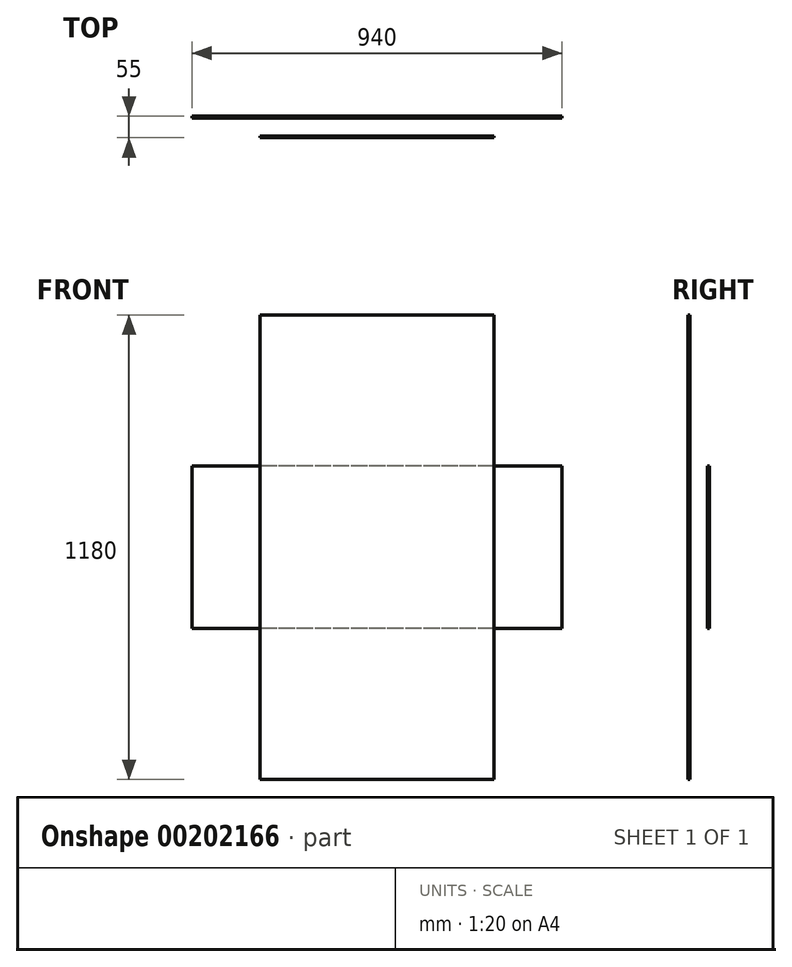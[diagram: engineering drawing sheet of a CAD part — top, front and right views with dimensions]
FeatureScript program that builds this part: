
annotation { "Feature Type Name" : "Feature", "Feature Type Description" : "" }
export const myFeature = defineFeature(function(context is Context, id is Id, definition is map)
    precondition{}
    {
        {
            var Q0;
            Q0=qCreatedBy(makeId("Front.planeOp"),FACE);
            var sketch = newSketch(context, id + "F0", { "sketchPlane" : qUnion([Q0])});
            skLineSegment(sketch, "E0.bottom", {"start": v(470, 206) * mm, "end": v(-470, 206) * mm});
            skLineSegment(sketch, "E0.top", {"start": v(470, -206) * mm, "end": v(-470, -206) * mm});
            skLineSegment(sketch, "E0.left", {"start": v(470, 206) * mm, "end": v(470, -206) * mm});
            skLineSegment(sketch, "E0.right", {"start": v(-470, 206) * mm, "end": v(-470, -206) * mm});
            skPoint(sketch, "E0.middle", {"position": v(0, 0) * mm});
            skSolve(sketch);
        }
        {
            var Q0;
            Q0=qSketchRegion(id+"F0",true);
            extrude(context, id + "F1", {"entities" : qUnion([Q0]), "depth" : 5 * mm});
        }
        {
            var Q0;
            Q0=qCreatedBy(makeId("Front.planeOp"),FACE);
            cPlane(context, id + "F2", {"entities" : qUnion([Q0]), "cplaneType" : CPlaneType.OFFSET, "offset" : 50 * mm, "width" : 150 * mm, "height" : 150 * mm});
        }
        {
            var Q0;
            Q0=qCreatedBy(id+"F2.planeOp",FACE);
            var sketch = newSketch(context, id + "F3", { "sketchPlane" : qUnion([Q0])});
            skLineSegment(sketch, "E1.bottom", {"start": v(297.5, 590) * mm, "end": v(-297.5, 590) * mm});
            skLineSegment(sketch, "E1.top", {"start": v(297.5, -590) * mm, "end": v(-297.5, -590) * mm});
            skLineSegment(sketch, "E1.left", {"start": v(297.5, 590) * mm, "end": v(297.5, -590) * mm});
            skLineSegment(sketch, "E1.right", {"start": v(-297.5, 590) * mm, "end": v(-297.5, -590) * mm});
            skPoint(sketch, "E1.middle", {"position": v(0, 0) * mm});
            skSolve(sketch);
        }
        {
            var Q0;
            Q0=qSketchRegion(id+"F3",true);
            extrude(context, id + "F4", {"entities" : qUnion([Q0]), "depth" : 5 * mm});
        }
    });
